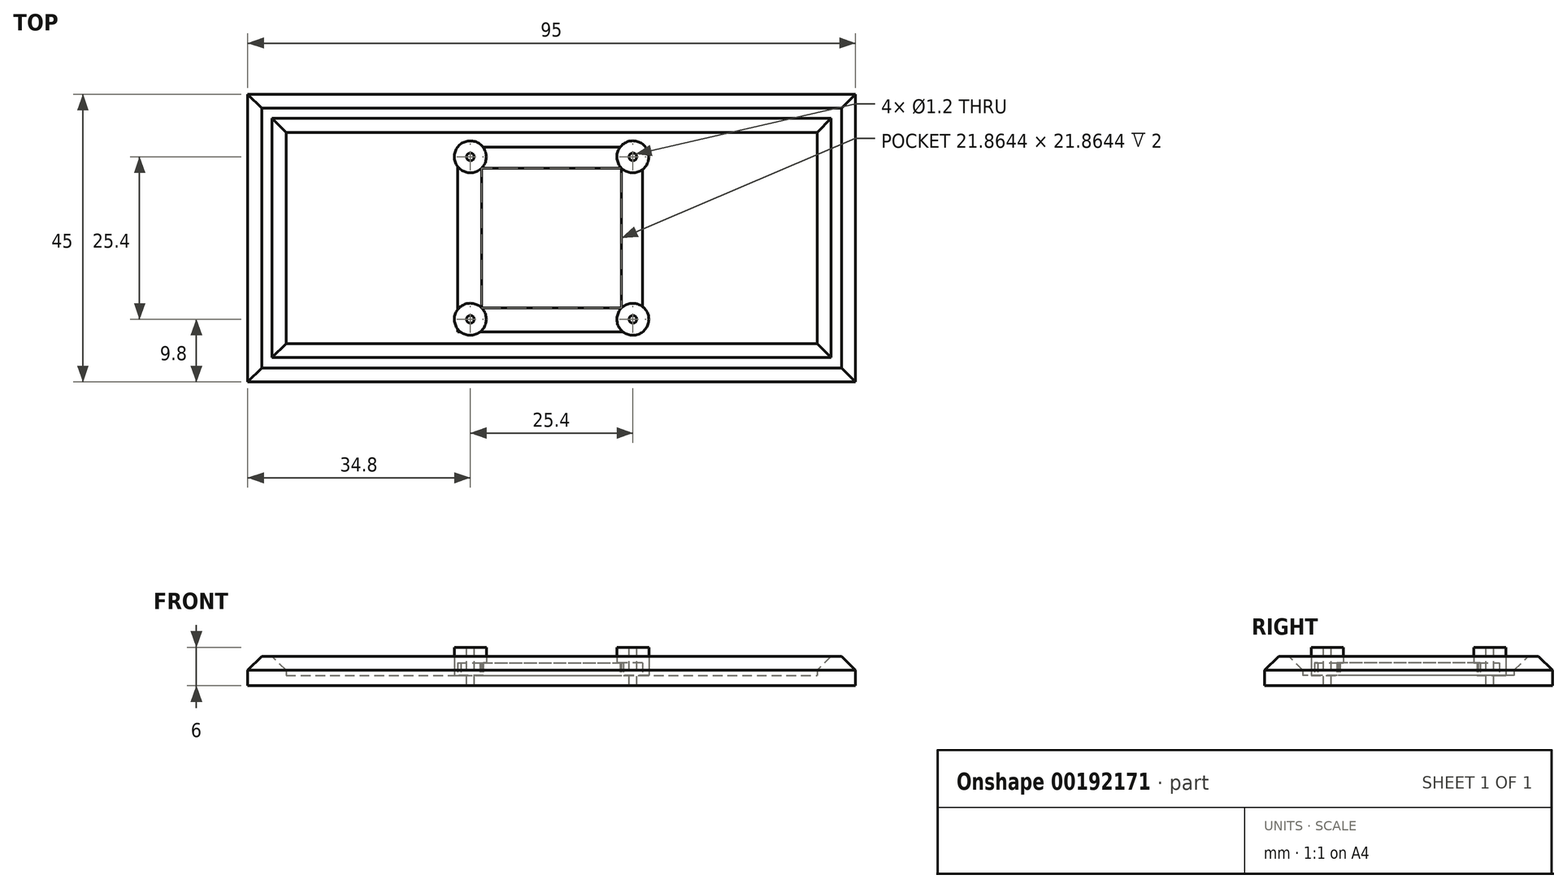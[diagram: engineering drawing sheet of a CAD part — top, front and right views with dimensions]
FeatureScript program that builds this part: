
annotation { "Feature Type Name" : "Feature", "Feature Type Description" : "" }
export const myFeature = defineFeature(function(context is Context, id is Id, definition is map)
    precondition{}
    {
        {
            var Q0;
            Q0=qCreatedBy(makeId("Top.planeOp"),FACE);
            var sketch = newSketch(context, id + "F0", { "sketchPlane" : qUnion([Q0])});
            skLineSegment(sketch, "E0.bottom", {"start": v(12.7, 12.7) * mm, "end": v(-12.7, 12.7) * mm, "construction": true});
            skLineSegment(sketch, "E0.top", {"start": v(12.7, -12.7) * mm, "end": v(-12.7, -12.7) * mm, "construction": true});
            skLineSegment(sketch, "E0.left", {"start": v(12.7, 12.7) * mm, "end": v(12.7, -12.7) * mm, "construction": true});
            skLineSegment(sketch, "E0.right", {"start": v(-12.7, 12.7) * mm, "end": v(-12.7, -12.7) * mm, "construction": true});
            skPoint(sketch, "E0.middle", {"position": v(0, 0) * mm});
            skCircle(sketch, "E1", {"center": v(-12.7, 12.7) * mm, "radius": 2.5 * mm});
            skCircle(sketch, "E2", {"center": v(-12.7, -12.7) * mm, "radius": 2.5 * mm});
            skCircle(sketch, "E3", {"center": v(12.7, -12.7) * mm, "radius": 2.5 * mm});
            skCircle(sketch, "E4", {"center": v(12.7, 12.7) * mm, "radius": 2.5 * mm});
            skLineSegment(sketch, "E5.bottom", {"start": v(44.5, 22.5) * mm, "end": v(-44.5, 22.5) * mm});
            skLineSegment(sketch, "E5.top", {"start": v(44.5, -22.5) * mm, "end": v(-44.5, -22.5) * mm});
            skLineSegment(sketch, "E5.left", {"start": v(44.5, 22.5) * mm, "end": v(44.5, -22.5) * mm});
            skLineSegment(sketch, "E5.right", {"start": v(-44.5, 22.5) * mm, "end": v(-44.5, -22.5) * mm});
            skLineSegment(sketch, "E6.bottom", {"start": v(44.5, 22.5) * mm, "end": v(47.5, 22.5) * mm});
            skLineSegment(sketch, "E6.top", {"start": v(44.5, -22.5) * mm, "end": v(47.5, -22.5) * mm});
            skLineSegment(sketch, "E6.right", {"start": v(47.5, 22.5) * mm, "end": v(47.5, -22.5) * mm});
            skLineSegment(sketch, "E7", {"start": v(0, 0) * mm, "end": v(0, -44.7) * mm, "construction": true});
            skLineSegment(sketch, "E8.MirrorCS", {"start": v(-44.5, -22.5) * mm, "end": v(44.5, -22.5) * mm});
            skLineSegment(sketch, "E9.MirrorCS", {"start": v(-44.5, 22.5) * mm, "end": v(44.5, 22.5) * mm});
            skLineSegment(sketch, "E10.MirrorCS", {"start": v(-47.5, 22.5) * mm, "end": v(-47.5, -22.5) * mm});
            skLineSegment(sketch, "E11.MirrorCS", {"start": v(-44.5, -22.5) * mm, "end": v(-47.5, -22.5) * mm});
            skLineSegment(sketch, "E12.MirrorCS", {"start": v(-44.5, 22.5) * mm, "end": v(-47.5, 22.5) * mm});
            skSolve(sketch);
        }
        {
            var Q0;
            Q0 = qSketchRegion(id + "F0", true);
            var Q1;
            Q1=makeQuery(id+"F0.imprint","IMPRINT",FACE,{"disambiguationData":[TD([[makeQuery(id+"F0.imprint","IMPRINT",EDGE,{"derivedFrom":sQuery(id+"F0.wireOp",EDGE,"E1")}),1.0]])]});
            var Q2;
            Q2=makeQuery(id+"F0.imprint","IMPRINT",FACE,{"disambiguationData":[TD([[makeQuery(id+"F0.imprint","IMPRINT",EDGE,{"derivedFrom":sQuery(id+"F0.wireOp",EDGE,"E4")}),1.0]])]});
            var Q3;
            Q3=makeQuery(id+"F0.imprint","IMPRINT",FACE,{"disambiguationData":[TD([[makeQuery(id+"F0.imprint","IMPRINT",EDGE,{"derivedFrom":sQuery(id+"F0.wireOp",EDGE,"E3")}),1.0]])]});
            var Q4;
            Q4=makeQuery(id+"F0.imprint","IMPRINT",FACE,{"disambiguationData":[TD([[makeQuery(id+"F0.imprint","IMPRINT",EDGE,{"derivedFrom":sQuery(id+"F0.wireOp",EDGE,"E2")}),1.0]])]});
            extrude(context, id + "F1", {"entities" : qUnion([Q0, Q1, Q2, Q3, Q4]), "depth" : 1.6 * mm});
        }
        {
            var Q0;
            Q0=makeQuery(id+"F0.imprint","IMPRINT",FACE,{"disambiguationData":[TD([[makeQuery(id+"F0.imprint","IMPRINT",EDGE,{"derivedFrom":sQuery(id+"F0.wireOp",EDGE,"E2")}),1.0]])]});
            var Q1;
            Q1=makeQuery(id+"F0.imprint","IMPRINT",FACE,{"disambiguationData":[TD([[makeQuery(id+"F0.imprint","IMPRINT",EDGE,{"derivedFrom":sQuery(id+"F0.wireOp",EDGE,"E1")}),1.0]])]});
            var Q2;
            Q2=makeQuery(id+"F0.imprint","IMPRINT",FACE,{"disambiguationData":[TD([[makeQuery(id+"F0.imprint","IMPRINT",EDGE,{"derivedFrom":sQuery(id+"F0.wireOp",EDGE,"E3")}),1.0]])]});
            var Q3;
            Q3=makeQuery(id+"F0.imprint","IMPRINT",FACE,{"disambiguationData":[TD([[makeQuery(id+"F0.imprint","IMPRINT",EDGE,{"derivedFrom":sQuery(id+"F0.wireOp",EDGE,"E4")}),1.0]])]});
            extrude(context, id + "F2", {"entities" : qUnion([Q0, Q1, Q2, Q3]), "operationType" : NewBodyOperationType.ADD, "depth" : 6 * mm});
        }
        {
            var Q0;
            Q0=makeQuery(id+"F1.opExtrude","CAP_FACE",FACE,{"disambiguationData":[OSD([sQuery(id+"F0.wireOp",EDGE,"E6.bottom"),sQuery(id+"F0.wireOp",EDGE,"E6.top"),sQuery(id+"F0.wireOp",EDGE,"E6.right"),sQuery(id+"F0.wireOp",EDGE,"E8.MirrorCS"),sQuery(id+"F0.wireOp",EDGE,"E9.MirrorCS"),sQuery(id+"F0.wireOp",EDGE,"E10.MirrorCS"),sQuery(id+"F0.wireOp",EDGE,"E11.MirrorCS"),sQuery(id+"F0.wireOp",EDGE,"E12.MirrorCS")])],"isStart":false});
            var sketch = newSketch(context, id + "F3", { "sketchPlane" : qUnion([Q0])});
            skLineSegment(sketch, "E13.bottom", {"start": v(-47.5, 22.5) * mm, "end": v(47.5, 22.5) * mm});
            skLineSegment(sketch, "E13.top", {"start": v(-47.5, 16.5) * mm, "end": v(47.5, 16.5) * mm});
            skLineSegment(sketch, "E13.left", {"start": v(-47.5, 22.5) * mm, "end": v(-47.5, 16.5) * mm});
            skLineSegment(sketch, "E13.right", {"start": v(47.5, 22.5) * mm, "end": v(47.5, 16.5) * mm});
            skLineSegment(sketch, "E14.bottom", {"start": v(-47.5, -22.5) * mm, "end": v(47.5, -22.5) * mm});
            skLineSegment(sketch, "E14.top", {"start": v(-47.5, -16.5) * mm, "end": v(47.5, -16.5) * mm});
            skLineSegment(sketch, "E14.left", {"start": v(-47.5, -22.5) * mm, "end": v(-47.5, -16.5) * mm});
            skLineSegment(sketch, "E14.right", {"start": v(47.5, -22.5) * mm, "end": v(47.5, -16.5) * mm});
            skLineSegment(sketch, "E15.bottom", {"start": v(47.5, -22.5) * mm, "end": v(41.5, -22.5) * mm});
            skLineSegment(sketch, "E15.top", {"start": v(47.5, 22.5) * mm, "end": v(41.5, 22.5) * mm});
            skLineSegment(sketch, "E15.left", {"start": v(47.5, -22.5) * mm, "end": v(47.5, 22.5) * mm});
            skLineSegment(sketch, "E15.right", {"start": v(41.5, -22.5) * mm, "end": v(41.5, 22.5) * mm});
            skLineSegment(sketch, "E16.bottom", {"start": v(-47.5, 22.5) * mm, "end": v(-41.5, 22.5) * mm});
            skLineSegment(sketch, "E16.top", {"start": v(-47.5, -22.5) * mm, "end": v(-41.5, -22.5) * mm});
            skLineSegment(sketch, "E16.left", {"start": v(-47.5, 22.5) * mm, "end": v(-47.5, -22.5) * mm});
            skLineSegment(sketch, "E16.right", {"start": v(-41.5, 22.5) * mm, "end": v(-41.5, -22.5) * mm});
            skSolve(sketch);
        }
        {
            var Q0;
            Q0 = qSketchRegion(id + "F3", true);
            extrude(context, id + "F4", {"entities" : qUnion([Q0]), "operationType" : NewBodyOperationType.ADD, "depth" : 3 * mm});
        }
        {
            var Q0;
            Q0=makeQuery(id+"F1.opExtrude","CAP_FACE",FACE,{"disambiguationData":[OSD([sQuery(id+"F0.wireOp",EDGE,"E6.bottom"),sQuery(id+"F0.wireOp",EDGE,"E6.top"),sQuery(id+"F0.wireOp",EDGE,"E6.right"),sQuery(id+"F0.wireOp",EDGE,"E8.MirrorCS"),sQuery(id+"F0.wireOp",EDGE,"E9.MirrorCS"),sQuery(id+"F0.wireOp",EDGE,"E10.MirrorCS"),sQuery(id+"F0.wireOp",EDGE,"E11.MirrorCS"),sQuery(id+"F0.wireOp",EDGE,"E12.MirrorCS")])],"isStart":false});
            var sketch = newSketch(context, id + "F5", { "sketchPlane" : qUnion([Q0])});
            skLineSegment(sketch, "E17.bottom", {"start": v(-14.7, 14.2) * mm, "end": v(14.2, 14.2) * mm});
            skLineSegment(sketch, "E17.top", {"start": v(-14.7, -14.7) * mm, "end": v(14.2, -14.7) * mm});
            skLineSegment(sketch, "E17.left", {"start": v(-14.7, 14.2) * mm, "end": v(-14.7, -14.7) * mm});
            skLineSegment(sketch, "E17.right", {"start": v(14.2, 14.2) * mm, "end": v(14.2, -14.7) * mm});
            skLineSegment(sketch, "E18.bottom", {"start": v(-10.93, 10.93) * mm, "end": v(10.93, 10.93) * mm});
            skLineSegment(sketch, "E18.top", {"start": v(-10.93, -10.93) * mm, "end": v(10.93, -10.93) * mm});
            skLineSegment(sketch, "E18.left", {"start": v(-10.93, 10.93) * mm, "end": v(-10.93, -10.93) * mm});
            skLineSegment(sketch, "E18.right", {"start": v(10.93, 10.93) * mm, "end": v(10.93, -10.93) * mm});
            skSolve(sketch);
        }
        {
            var Q0;
            Q0 = qSketchRegion(id + "F5", true);
            extrude(context, id + "F6", {"entities" : qUnion([Q0]), "operationType" : NewBodyOperationType.ADD, "depth" : 2 * mm});
        }
        {
            var Q0;
            Q0=makeQuery(id+"F2.opExtrude","CAP_FACE",FACE,{"disambiguationData":[OSD([sQuery(id+"F0.wireOp",EDGE,"E1")])],"isStart":false});
            var sketch = newSketch(context, id + "F7", { "sketchPlane" : qUnion([Q0])});
            skCircle(sketch, "E19", {"center": v(-12.7, 12.7) * mm, "radius": 0.6 * mm});
            skCircle(sketch, "E20", {"center": v(12.7, 12.7) * mm, "radius": 0.6 * mm});
            skCircle(sketch, "E21", {"center": v(12.7, -12.7) * mm, "radius": 0.6 * mm});
            skCircle(sketch, "E22", {"center": v(-12.7, -12.7) * mm, "radius": 0.6 * mm});
            skSolve(sketch);
        }
        {
            var Q0;
            Q0 = qSketchRegion(id + "F7", true);
            extrude(context, id + "F8", {"entities" : qUnion([Q0]), "operationType" : NewBodyOperationType.REMOVE, "oppositeDirection" : true, "depth" : 6 * mm});
        }
        {
            var Q0;
            Q0=makeQuery(id+"F4.opExtrude","CAP_EDGE",EDGE,{"disambiguationData":[OSD([sQuery(id+"F3.wireOp",EDGE,"E13.top")])],"isStart":false});
            var Q1;
            Q1=makeQuery(id+"F4.opExtrude","CAP_EDGE",EDGE,{"disambiguationData":[OSD([sQuery(id+"F3.wireOp",EDGE,"E16.right")])],"isStart":false});
            var Q2;
            Q2=makeQuery(id+"F4.opExtrude","CAP_EDGE",EDGE,{"disambiguationData":[OSD([sQuery(id+"F3.wireOp",EDGE,"E16.left")])],"isStart":false});
            var Q3;
            Q3=makeQuery(id+"F4.opExtrude","CAP_EDGE",EDGE,{"disambiguationData":[OSD([sQuery(id+"F3.wireOp",EDGE,"E13.bottom"),sQuery(id+"F3.wireOp",EDGE,"E15.top"),sQuery(id+"F3.wireOp",EDGE,"E16.bottom")])],"isStart":false});
            var Q4;
            Q4=makeQuery(id+"F4.opExtrude","CAP_EDGE",EDGE,{"disambiguationData":[OSD([sQuery(id+"F3.wireOp",EDGE,"E14.bottom"),sQuery(id+"F3.wireOp",EDGE,"E15.bottom"),sQuery(id+"F3.wireOp",EDGE,"E16.top")])],"isStart":false});
            var Q5;
            Q5=makeQuery(id+"F4.opExtrude","CAP_EDGE",EDGE,{"disambiguationData":[OSD([sQuery(id+"F3.wireOp",EDGE,"E15.left")])],"isStart":false});
            var Q6;
            Q6=makeQuery(id+"F4.opExtrude","CAP_EDGE",EDGE,{"disambiguationData":[OSD([sQuery(id+"F3.wireOp",EDGE,"E15.right")])],"isStart":false});
            var Q7;
            Q7=makeQuery(id+"F4.opExtrude","CAP_EDGE",EDGE,{"disambiguationData":[OSD([sQuery(id+"F3.wireOp",EDGE,"E14.top")])],"isStart":false});
            chamfer(context, id + "F9", {"entities" : qUnion([Q0, Q1, Q2, Q3, Q4, Q5, Q6, Q7]), "width" : 2.2 * mm, "tangentPropagation" : true});
        }
    });
